# Revit family: Alutech_W62_Horizontal_3
name_source: partatom
category: Windows
units: mm (PartAtom-declared; Revit-internal decimal feet)

## family parameters
Always vertical = Yes
Classification Number = 23.30.20.00
Cut with Voids When Loaded = No
Host = Wall
Room Calculation Point = No
Shared = No

## types (1)
- 2000x1500
    Air permeability = Class 4
    Analytic Construction = <Нет>
    COBIe Type Category = Windows
    Construction Type = Window,Triple_Vent,Triple_Fixed
    Date of publishing = 2017-02-08
    Design country = Belarus
    Edition number = 1.0
    Facade insert unit = yes
    Fittings = <By Category>
    Frame = <By Category>
    Gap to shell construction = 10 mm  [stored 0.0328084 ft]
    Glass = <By Category>
    Glazing = Glass
    Height = 2000 mm  [stored 6.56168 ft]
    IFC Classification = Window
    Manufacturer country = Belarus
    Manufacturer name = AluminTechno LLC
    Material = Aluminium
    Material frame = Aluminium
    NBS Reference Code = 59-97-02
    NBS Reference Description = Aluminium Window Units
    Nominal height = 0
    Nominal width = 0
    Opening type = Inward-opening, side-hung (SH), turn/tilt (TT), bottom-hung (BH), tilt-befort-turn (TbT)
    Product family = Aluminium windows (ALT.W62)
    Product group = Windows and Doors
    Reveal sill = 0 mm  [stored 0 ft]
    Reveal, lintel and sides = 20 mm  [stored 0.0656168 ft]
    Rough Height = 2020 mm  [stored 6.6273 ft]
    Rough Width = 1520 mm  [stored 4.98688 ft]
    Sill height (default) = 800 mm  [stored 2.62467 ft]
    Sound insulation = -
    Thermal insulation = Uf to 2,83 W/(m2K)
    UNSPSC Code = 301716
    Uniclass 2.0 Code = SS-25-30-95
    Uniclass 2.0 Description = Window Systems
    Wall Closure = By host
    Watertightness = Class E900
    Weight Net (Kg) = 0
    Width = 1500 mm  [stored 4.92126 ft]
    Wind load resistance = Class C4
    Window position in wall = 55 mm  [stored 0.180446 ft]

note: [stored X ft] marks values corroborated as IEEE doubles in the binary element streams (Revit-internal decimal feet)
